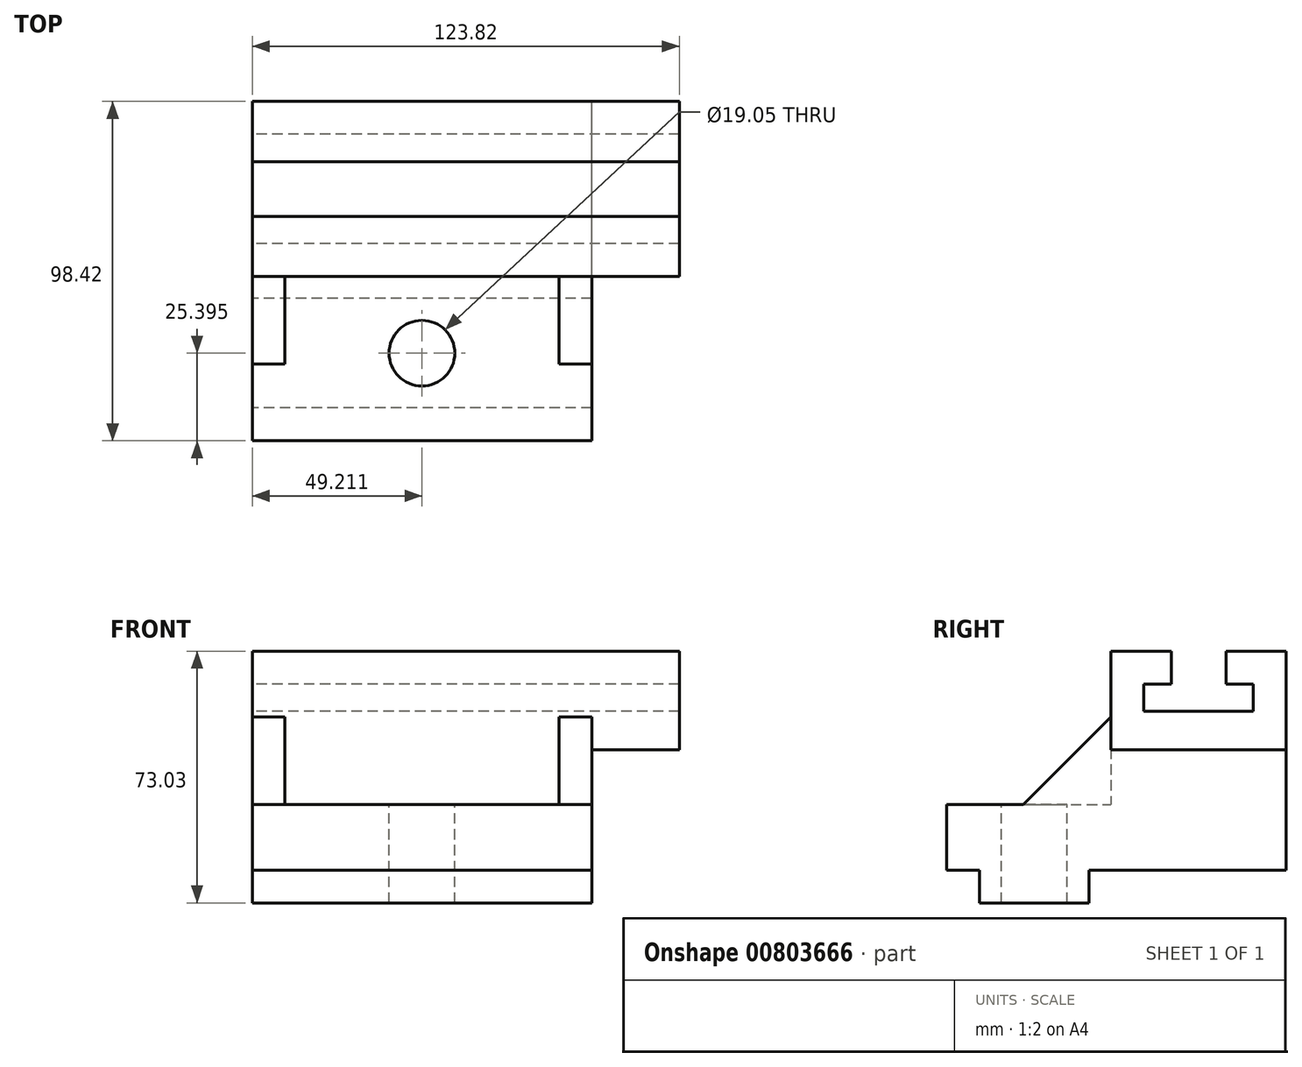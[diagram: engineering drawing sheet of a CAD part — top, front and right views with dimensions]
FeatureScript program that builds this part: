
annotation { "Feature Type Name" : "Feature", "Feature Type Description" : "" }
export const myFeature = defineFeature(function(context is Context, id is Id, definition is map)
    precondition{}
    {
        {
            var Q0;
            Q0=qCreatedBy(makeId("Front.planeOp"),FACE);
            var sketch = newSketch(context, id + "F0", { "sketchPlane" : qUnion([Q0])});
            skLineSegment(sketch, "E0.bottom", {"start": v(-32.97, 1.92) * mm, "end": v(65.45, 1.92) * mm});
            skLineSegment(sketch, "E0.top", {"start": v(-32.97, -17.13) * mm, "end": v(65.45, -17.13) * mm});
            skLineSegment(sketch, "E0.left", {"start": v(-32.97, 1.92) * mm, "end": v(-32.97, -17.13) * mm});
            skLineSegment(sketch, "E0.right", {"start": v(65.45, 1.92) * mm, "end": v(65.45, -17.13) * mm});
            skSolve(sketch);
        }
        {
            var Q0;
            Q0 = qSketchRegion(id + "F0", true);
            extrude(context, id + "F1", {"entities" : qUnion([Q0]), "depth" : 98.42 * mm, "offsetDistance" : 25.4 * mm});
        }
        {
            var Q0;
            Q0=makeQuery(id+"F1.opExtrude","SWEPT_FACE",FACE,{"disambiguationData":[OSD([sQuery(id+"F0.wireOp",EDGE,"E0.top")])]});
            var sketch = newSketch(context, id + "F2", { "sketchPlane" : qUnion([Q0])});
            skLineSegment(sketch, "E1", {"start": v(65.45, 98.43) * mm, "end": v(65.45, 88.9) * mm});
            skLineSegment(sketch, "E2", {"start": v(65.45, 88.9) * mm, "end": v(65.45, 57.15) * mm});
            skLineSegment(sketch, "E3", {"start": v(65.45, 57.15) * mm, "end": v(-32.97, 57.15) * mm});
            skLineSegment(sketch, "E4", {"start": v(65.45, 88.9) * mm, "end": v(-32.97, 88.9) * mm});
            skLineSegment(sketch, "E5", {"start": v(-32.97, 88.9) * mm, "end": v(-32.97, 57.15) * mm});
            skSolve(sketch);
        }
        {
            var Q0;
            Q0 = qSketchRegion(id + "F2", true);
            extrude(context, id + "F3", {"entities" : qUnion([Q0]), "operationType" : NewBodyOperationType.ADD, "depth" : 9.52 * mm, "offsetDistance" : 25.4 * mm});
        }
        {
            var Q0;
            Q0=makeQuery(id+"F1.opExtrude","SWEPT_FACE",FACE,{"disambiguationData":[OSD([sQuery(id+"F0.wireOp",EDGE,"E0.bottom")])]});
            var sketch = newSketch(context, id + "F4", { "sketchPlane" : qUnion([Q0])});
            skLineSegment(sketch, "E6", {"start": v(-32.97, -98.43) * mm, "end": v(16.24, -98.43) * mm});
            skLineSegment(sketch, "E7", {"start": v(16.24, -98.43) * mm, "end": v(16.24, -73.03) * mm});
            skCircle(sketch, "E8", {"center": v(16.24, -73.03) * mm, "radius": 9.53 * mm});
            skSolve(sketch);
        }
        {
            var Q0;
            Q0 = qSketchRegion(id + "F4", true);
            extrude(context, id + "F5", {"entities" : qUnion([Q0]), "operationType" : NewBodyOperationType.REMOVE, "oppositeDirection" : true, "depth" : 58.93 * mm, "offsetDistance" : 25.4 * mm});
        }
        {
            var Q0;
            Q0=makeQuery(id+"F1.opExtrude","SWEPT_FACE",FACE,{"disambiguationData":[OSD([sQuery(id+"F0.wireOp",EDGE,"E0.bottom")])]});
            var sketch = newSketch(context, id + "F6", { "sketchPlane" : qUnion([Q0])});
            skLineSegment(sketch, "E9", {"start": v(-32.97, 0) * mm, "end": v(-32.97, -50.8) * mm});
            skLineSegment(sketch, "E10", {"start": v(-32.97, -50.8) * mm, "end": v(65.45, -50.8) * mm});
            skSolve(sketch);
        }
        {
            var Q0;
            Q0 = qSketchRegion(id + "F6", true);
            var Q1;
            Q1=makeQuery(id+"F6.imprint","IMPRINT",FACE,{"disambiguationData":[TD([[makeQuery(id+"F6.imprint","IMPRINT",EDGE,{"derivedFrom":sQuery(id+"F6.wireOp",EDGE,"E9")}),-1.0]])]});
            extrude(context, id + "F7", {"entities" : qUnion([Q0, Q1]), "operationType" : NewBodyOperationType.ADD, "depth" : 44.45 * mm, "offsetDistance" : 25.4 * mm});
        }
        {
            var Q0;
            Q0=makeQuery(id+"F7.opExtrude","CAP_FACE",FACE,{"disambiguationData":[OSD([sQuery(id+"F0.wireOp",EDGE,"E0.bottom"),sQuery(id+"F0.wireOp",EDGE,"E0.right"),sQuery(id+"F6.wireOp",EDGE,"E9"),sQuery(id+"F6.wireOp",EDGE,"E10")])],"isStart":false});
            var sketch = newSketch(context, id + "F8", { "sketchPlane" : qUnion([Q0])});
            skLineSegment(sketch, "E11", {"start": v(-32.97, -50.8) * mm, "end": v(-32.97, -33.34) * mm});
            skLineSegment(sketch, "E12", {"start": v(-32.97, -33.34) * mm, "end": v(65.45, -33.34) * mm});
            skLineSegment(sketch, "E13", {"start": v(-32.97, -33.34) * mm, "end": v(-32.97, -17.46) * mm});
            skLineSegment(sketch, "E14", {"start": v(-32.97, -17.46) * mm, "end": v(65.45, -17.46) * mm});
            skSolve(sketch);
        }
        {
            var Q0;
            Q0 = qSketchRegion(id + "F8", true);
            var Q1;
            {var subQ0=sQuery(id+"F8.wireOp",EDGE,"E12");Q1=makeQuery(id+"F8.imprint","IMPRINT",FACE,{"disambiguationData":[TD([[makeQuery(id+"F8.imprint","IMPRINT",EDGE,{"derivedFrom":subQ0}),1.0]])]});}
            extrude(context, id + "F9", {"entities" : qUnion([Q0, Q1]), "operationType" : NewBodyOperationType.REMOVE, "oppositeDirection" : true, "depth" : 17.46 * mm, "offsetDistance" : 25.4 * mm});
        }
        {
            var Q0;
            Q0=makeQuery(id+"F7.boolean.opBoolean","MERGE",FACE,{"derivedFrom":[makeQuery(id+"F3.boolean.opBoolean","MERGE",FACE,{"derivedFrom":[makeQuery(id+"F1.opExtrude","SWEPT_FACE",FACE,{"disambiguationData":[OSD([sQuery(id+"F0.wireOp",EDGE,"E0.left")])]}),makeQuery(id+"F3.opExtrude","SWEPT_FACE",FACE,{"disambiguationData":[OSD([sQuery(id+"F2.wireOp",EDGE,"E5")])]})]}),makeQuery(id+"F7.opExtrude","SWEPT_FACE",FACE,{"disambiguationData":[OSD([sQuery(id+"F6.wireOp",EDGE,"E9")])]})]});
            var sketch = newSketch(context, id + "F10", { "sketchPlane" : qUnion([Q0])});
            skLineSegment(sketch, "E15", {"start": v(33.34, 28.9) * mm, "end": v(41.28, 28.9) * mm});
            skLineSegment(sketch, "E16", {"start": v(17.46, 28.9) * mm, "end": v(9.53, 28.9) * mm});
            skLineSegment(sketch, "E17", {"start": v(9.53, 28.9) * mm, "end": v(9.53, 36.84) * mm});
            skLineSegment(sketch, "E18", {"start": v(9.53, 36.84) * mm, "end": v(41.28, 36.84) * mm});
            skLineSegment(sketch, "E19", {"start": v(41.28, 36.84) * mm, "end": v(41.28, 28.9) * mm});
            skSolve(sketch);
        }
        {
            var Q0;
            Q0 = qSketchRegion(id + "F10", true);
            var Q1;
            {var subQ0=sQuery(id+"F10.wireOp",EDGE,"E16");Q1=makeQuery(id+"F10.imprint","IMPRINT",FACE,{"disambiguationData":[TD([[makeQuery(id+"F10.imprint","IMPRINT",EDGE,{"derivedFrom":subQ0}),-1.0]])]});}
            var Q2;
            {var subQ0=sQuery(id+"F10.wireOp",EDGE,"E15");Q2=makeQuery(id+"F10.imprint","IMPRINT",FACE,{"disambiguationData":[TD([[makeQuery(id+"F10.imprint","IMPRINT",EDGE,{"derivedFrom":subQ0}),1.0]])]});}
            extrude(context, id + "F11", {"entities" : qUnion([Q0, Q1, Q2]), "operationType" : NewBodyOperationType.REMOVE, "oppositeDirection" : true, "depth" : 104.4 * mm, "offsetDistance" : 25.4 * mm});
        }
        {
            var Q0;
            {var subQ0=sQuery(id+"F0.wireOp",EDGE,"E0.right");Q0=makeQuery(id+"F7.boolean.opBoolean","MERGE",FACE,{"derivedFrom":[makeQuery(id+"F3.boolean.opBoolean","MERGE",FACE,{"derivedFrom":[makeQuery(id+"F1.opExtrude","SWEPT_FACE",FACE,{"disambiguationData":[OSD([subQ0])]}),makeQuery(id+"F3.opExtrude","SWEPT_FACE",FACE,{"disambiguationData":[OSD([sQuery(id+"F2.wireOp",EDGE,"E2")])]})]}),makeQuery(id+"F7.opExtrude","SWEPT_FACE",FACE,{"disambiguationData":[OSD([sQuery(id+"F0.wireOp",EDGE,"E0.bottom"),subQ0])]})]});}
            var sketch = newSketch(context, id + "F12", { "sketchPlane" : qUnion([Q0])});
            skLineSegment(sketch, "E20", {"start": v(-50.8, 46.37) * mm, "end": v(-50.8, 17.8) * mm});
            skLineSegment(sketch, "E21", {"start": v(-50.8, 17.8) * mm, "end": v(0, 17.8) * mm});
            skSolve(sketch);
        }
        {
            var Q0;
            Q0 = qSketchRegion(id + "F12", true);
            var Q1;
            Q1=makeQuery(id+"F12.imprint","IMPRINT",FACE,{"disambiguationData":[TD([[makeQuery(id+"F12.imprint","IMPRINT",EDGE,{"derivedFrom":sQuery(id+"F12.wireOp",EDGE,"E20")}),1.0]])]});
            extrude(context, id + "F13", {"entities" : qUnion([Q0, Q1]), "operationType" : NewBodyOperationType.ADD, "depth" : 25.4 * mm, "offsetDistance" : 25.4 * mm});
        }
        {
            var Q0;
            Q0=makeQuery(id+"F13.boolean.opBoolean","MERGE",FACE,{"derivedFrom":[makeQuery(id+"F7.opExtrude","SWEPT_FACE",FACE,{"disambiguationData":[OSD([sQuery(id+"F6.wireOp",EDGE,"E10")])]}),makeQuery(id+"F13.opExtrude","SWEPT_FACE",FACE,{"disambiguationData":[OSD([sQuery(id+"F12.wireOp",EDGE,"E20")])]})]});
            var sketch = newSketch(context, id + "F14", { "sketchPlane" : qUnion([Q0])});
            skLineSegment(sketch, "E22", {"start": v(-32.97, 1.92) * mm, "end": v(-32.97, 27.32) * mm});
            skLineSegment(sketch, "E23", {"start": v(-32.97, 27.32) * mm, "end": v(-23.45, 27.32) * mm});
            skLineSegment(sketch, "E24", {"start": v(-23.45, 27.32) * mm, "end": v(-23.45, 1.92) * mm});
            skLineSegment(sketch, "E25", {"start": v(-23.45, 1.92) * mm, "end": v(-32.97, 1.92) * mm});
            skSolve(sketch);
        }
        {
            var Q0;
            Q0 = qSketchRegion(id + "F14", true);
            extrude(context, id + "F15", {"entities" : qUnion([Q0]), "operationType" : NewBodyOperationType.ADD, "depth" : 31.24 * mm, "offsetDistance" : 25.4 * mm});
        }
        {
            var Q0;
            Q0=makeQuery(id+"F15.opExtrude","SWEPT_FACE",FACE,{"disambiguationData":[OSD([sQuery(id+"F14.wireOp",EDGE,"E24")])]});
            var sketch = newSketch(context, id + "F16", { "sketchPlane" : qUnion([Q0])});
            skLineSegment(sketch, "E26", {"start": v(-50.8, 27.32) * mm, "end": v(-50.8, 1.92) * mm});
            skLineSegment(sketch, "E27", {"start": v(-50.8, 27.32) * mm, "end": v(-76.2, 1.92) * mm});
            skSolve(sketch);
        }
        {
            var Q0;
            Q0 = qSketchRegion(id + "F16", true);
            var Q1;
            {var subQ0=sQuery(id+"F16.wireOp",EDGE,"E27");Q1=makeQuery(id+"F16.imprint","IMPRINT",FACE,{"disambiguationData":[TD([[makeQuery(id+"F16.imprint","IMPRINT",EDGE,{"derivedFrom":subQ0}),-1.0]])]});}
            extrude(context, id + "F17", {"entities" : qUnion([Q0, Q1]), "operationType" : NewBodyOperationType.REMOVE, "oppositeDirection" : true, "depth" : 25.4 * mm, "offsetDistance" : 25.4 * mm});
        }
        {
            var Q0;
            Q0=makeQuery(id+"F13.boolean.opBoolean","MERGE",FACE,{"derivedFrom":[makeQuery(id+"F7.opExtrude","SWEPT_FACE",FACE,{"disambiguationData":[OSD([sQuery(id+"F6.wireOp",EDGE,"E10")])]}),makeQuery(id+"F13.opExtrude","SWEPT_FACE",FACE,{"disambiguationData":[OSD([sQuery(id+"F12.wireOp",EDGE,"E20")])]})]});
            var sketch = newSketch(context, id + "F18", { "sketchPlane" : qUnion([Q0])});
            skLineSegment(sketch, "E28", {"start": v(65.45, 1.92) * mm, "end": v(65.45, 27.32) * mm});
            skLineSegment(sketch, "E29", {"start": v(65.45, 27.32) * mm, "end": v(55.93, 27.32) * mm});
            skLineSegment(sketch, "E30", {"start": v(55.93, 27.32) * mm, "end": v(55.93, 1.92) * mm});
            skSolve(sketch);
        }
        {
            var Q0;
            Q0 = qSketchRegion(id + "F18", true);
            var Q1;
            {var subQ1=sQuery(id+"F18.wireOp",EDGE,"E29");Q1=makeQuery(id+"F18.imprint","IMPRINT",FACE,{"disambiguationData":[TD([[makeQuery(id+"F18.imprint","IMPRINT",EDGE,{"derivedFrom":subQ1}),1.0]])]});}
            extrude(context, id + "F19", {"entities" : qUnion([Q0, Q1]), "operationType" : NewBodyOperationType.ADD, "depth" : 39.88 * mm, "offsetDistance" : 25.4 * mm});
        }
        {
            var Q0;
            Q0=makeQuery(id+"F19.opExtrude","SWEPT_FACE",FACE,{"disambiguationData":[OSD([sQuery(id+"F18.wireOp",EDGE,"E30")])]});
            var sketch = newSketch(context, id + "F20", { "sketchPlane" : qUnion([Q0])});
            skLineSegment(sketch, "E31", {"start": v(50.8, 1.92) * mm, "end": v(50.8, 27.32) * mm});
            skLineSegment(sketch, "E32", {"start": v(50.8, 27.32) * mm, "end": v(76.2, 1.92) * mm});
            skSolve(sketch);
        }
        {
            var Q0;
            Q0 = qSketchRegion(id + "F20", true);
            var Q1;
            {var subQ0=sQuery(id+"F20.wireOp",EDGE,"E32");Q1=makeQuery(id+"F20.imprint","IMPRINT",FACE,{"disambiguationData":[TD([[makeQuery(id+"F20.imprint","IMPRINT",EDGE,{"derivedFrom":subQ0}),1.0]])]});}
            extrude(context, id + "F21", {"entities" : qUnion([Q0, Q1]), "operationType" : NewBodyOperationType.REMOVE, "oppositeDirection" : true, "depth" : 25.4 * mm, "offsetDistance" : 25.4 * mm});
        }
    });
